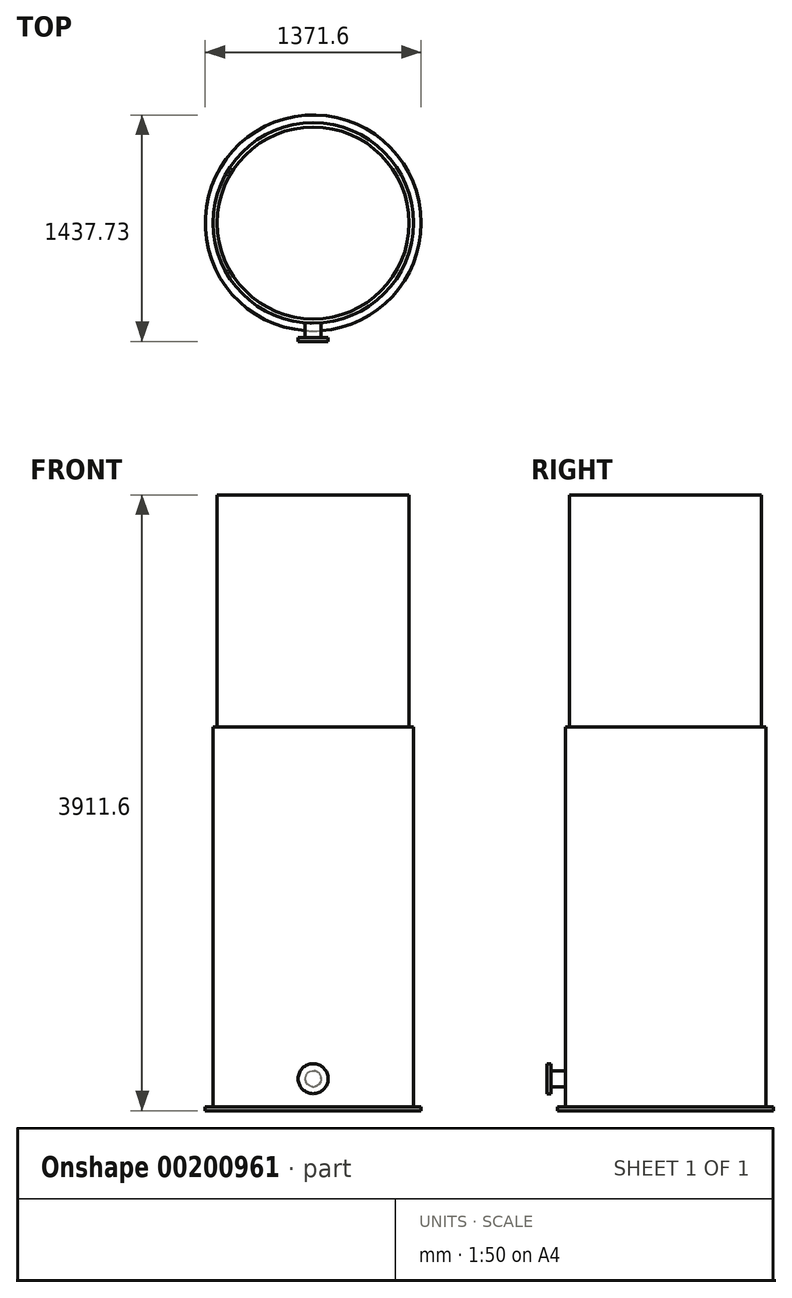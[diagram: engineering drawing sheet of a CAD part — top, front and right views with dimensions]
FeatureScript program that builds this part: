
annotation { "Feature Type Name" : "Feature", "Feature Type Description" : "" }
export const myFeature = defineFeature(function(context is Context, id is Id, definition is map)
    precondition{}
    {
        {
            var Q0;
            Q0=qCreatedBy(makeId("Top.planeOp"),FACE);
            var sketch = newSketch(context, id + "F0", { "sketchPlane" : qUnion([Q0])});
            skCircle(sketch, "E0", {"center": v(0, 0) * mm, "radius": 685.8 * mm});
            skCircle(sketch, "E1", {"center": v(0, 0) * mm, "radius": 609.6 * mm});
            skCircle(sketch, "E2", {"center": v(0, 0) * mm, "radius": 636.59 * mm});
            skSolve(sketch);
        }
        {
            var Q0;
            Q0=makeQuery(id+"F0.imprint","IMPRINT",FACE,{"disambiguationData":[TD([[makeQuery(id+"F0.imprint","IMPRINT",EDGE,{"derivedFrom":sQuery(id+"F0.wireOp",EDGE,"E1")}),1.0]])]});
            extrude(context, id + "F1", {"entities" : qUnion([Q0]), "depth" : 3911.6 * mm, "offsetDistance" : 25.4 * mm});
        }
        {
            var Q0;
            Q0=makeQuery(id+"F0.imprint","IMPRINT",FACE,{"disambiguationData":[TD([[makeQuery(id+"F0.imprint","IMPRINT",EDGE,{"derivedFrom":sQuery(id+"F0.wireOp",EDGE,"E1")}),-1.0]])]});
            extrude(context, id + "F2", {"entities" : qUnion([Q0]), "operationType" : NewBodyOperationType.ADD, "depth" : 2438.4 * mm, "offsetDistance" : 25.4 * mm});
        }
        {
            var Q0;
            Q0=makeQuery(id+"F0.imprint","IMPRINT",FACE,{"disambiguationData":[TD([[makeQuery(id+"F0.imprint","IMPRINT",EDGE,{"derivedFrom":sQuery(id+"F0.wireOp",EDGE,"E0")}),1.0]])]});
            extrude(context, id + "F3", {"entities" : qUnion([Q0]), "operationType" : NewBodyOperationType.ADD, "depth" : 25.4 * mm, "offsetDistance" : 25.4 * mm});
        }
        {
            var Q0;
            Q0=qCreatedBy(makeId("Right.planeOp"),FACE);
            var sketch = newSketch(context, id + "F4", { "sketchPlane" : qUnion([Q0])});
            skLineSegment(sketch, "E3", {"start": v(-751.93, 203.19) * mm, "end": v(-417.52, 203.19) * mm});
            skLineSegment(sketch, "E4", {"start": v(-751.93, 203.19) * mm, "end": v(-751.93, 298.44) * mm});
            skLineSegment(sketch, "E5", {"start": v(-751.93, 298.44) * mm, "end": v(-728.06, 298.44) * mm});
            skLineSegment(sketch, "E6", {"start": v(-728.06, 298.44) * mm, "end": v(-728.06, 253.99) * mm});
            skLineSegment(sketch, "E7", {"start": v(-728.06, 253.99) * mm, "end": v(-625.44, 253.99) * mm});
            skLineSegment(sketch, "E8", {"start": v(-625.44, 253.99) * mm, "end": v(-625.44, 203.19) * mm});
            skSolve(sketch);
        }
        {
            var Q0;
            {var subQ0=sQuery(id+"F4.wireOp",EDGE,"E4");Q0=makeQuery(id+"F4.imprint","IMPRINT",FACE,{"disambiguationData":[TD([[makeQuery(id+"F4.imprint","IMPRINT",EDGE,{"derivedFrom":subQ0}),-1.0]])]});}
            var Q1;
            Q1=sQuery(id+"F4.wireOp",EDGE,"E3");
            revolve(context, id + "F5", {"operationType" : NewBodyOperationType.ADD, "surfaceOperationType" : NewSurfaceOperationType.NEW, "entities" : qUnion([Q0]), "axis" : qUnion([Q1]), "revolveType" : RevolveType.FULL});
        }
    });
